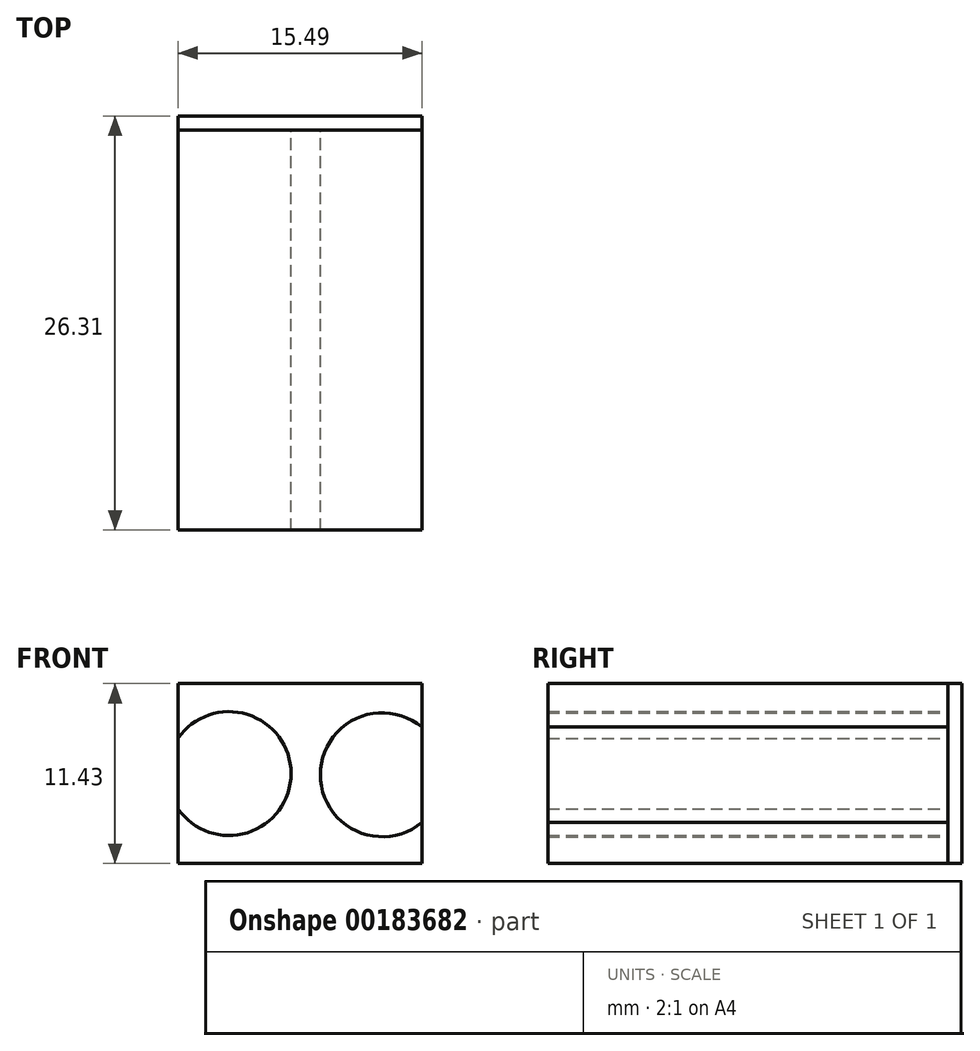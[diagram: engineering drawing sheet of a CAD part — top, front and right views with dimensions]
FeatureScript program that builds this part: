
annotation { "Feature Type Name" : "Feature", "Feature Type Description" : "" }
export const myFeature = defineFeature(function(context is Context, id is Id, definition is map)
    precondition{}
    {
        {
            var Q0;
            Q0=qCreatedBy(makeId("Front.planeOp"),FACE);
            var sketch = newSketch(context, id + "F0", { "sketchPlane" : qUnion([Q0])});
            skLineSegment(sketch, "E0.bottom", {"start": v(0, 0) * mm, "end": v(15.5, 0) * mm});
            skLineSegment(sketch, "E0.top", {"start": v(0, 11.43) * mm, "end": v(15.5, 11.43) * mm});
            skLineSegment(sketch, "E0.left", {"start": v(0, 0) * mm, "end": v(0, 11.43) * mm});
            skLineSegment(sketch, "E0.right", {"start": v(15.5, 0) * mm, "end": v(15.5, 11.43) * mm});
            skSolve(sketch);
        }
        {
            var Q0;
            Q0 = qSketchRegion(id + "F0", true);
            extrude(context, id + "F1", {"entities" : qUnion([Q0]), "depth" : 0.91 * mm});
        }
        {
            var Q0;
            Q0=makeQuery(id+"F1.opExtrude","CAP_FACE",FACE,{"disambiguationData":[OSD([sQuery(id+"F0.wireOp",EDGE,"E0.bottom"),sQuery(id+"F0.wireOp",EDGE,"E0.top"),sQuery(id+"F0.wireOp",EDGE,"E0.left"),sQuery(id+"F0.wireOp",EDGE,"E0.right")])],"isStart":false});
            var sketch = newSketch(context, id + "F2", { "sketchPlane" : qUnion([Q0])});
            skCircle(sketch, "E1", {"center": v(12.98, 5.64) * mm, "radius": 3.94 * mm});
            skCircle(sketch, "E2", {"center": v(3.24, 5.71) * mm, "radius": 3.94 * mm});
            skPoint(sketch, "E2.centerSnap0", {"position": v(0, 5.71) * mm});
            skSolve(sketch);
        }
        {
            var Q0;
            {var subQ1=makeQuery(id+"F1.opExtrude","CAP_EDGE",EDGE,{"disambiguationData":[OSD([sQuery(id+"F0.wireOp",EDGE,"E0.bottom")])],"isStart":false});Q0=makeQuery(id+"F2.imprint","IMPRINT",FACE,{"disambiguationData":[TD([[makeQuery(id+"F2.imprint","IMPRINT",EDGE,{"derivedFrom":subQ1}),1.0]])]});}
            extrude(context, id + "F3", {"entities" : qUnion([Q0]), "depth" : 25.4 * mm});
        }
    });
